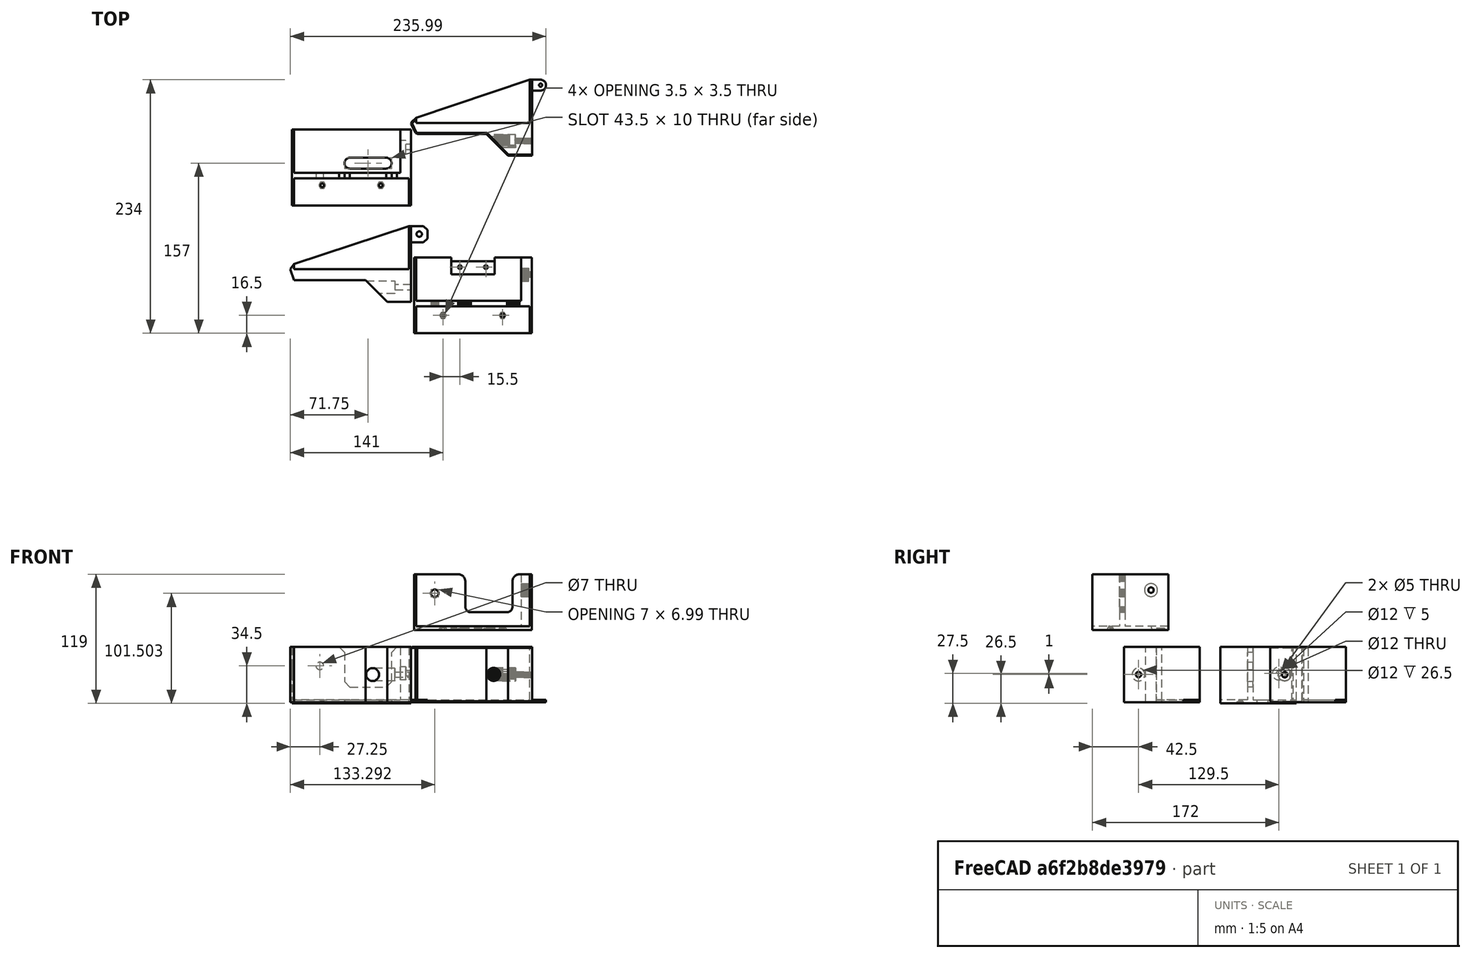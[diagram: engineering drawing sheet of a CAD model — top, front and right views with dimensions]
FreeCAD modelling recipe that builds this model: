
FCSTD DOCUMENT  (FreeCAD 0.19R24291 (Git))
Label: PRUSA-Black-PSU
License: All rights reserved
LicenseURL: http://en.wikipedia.org/wiki/All_rights_reserved
objects: Sketcher::SketchObject×19, PartDesign::Pocket×13, PartDesign::Pad×6, Part::Feature×4, Mesh::Feature×2, Part::Refine×2, PartDesign::Body×2, PartDesign::Chamfer×1
note: 67 computed .brp shape members not serialized (recipe doc carries the construction recipe); baked Part::Feature solids carry a one-line shape summary decoded from their .brp

FEATURE [Mesh::Feature] Top_Bracket_v5
FEATURE [Sketcher::SketchObject] Sketch
  FullyConstrained = true
  MapMode = 5
  Placement = pos=(0,0,0) rot=(1,0,0;1.5708rad)
  Support = -> [XZ_Plane]
  sketch-geometry (4):
    g0: LineSegment StartX=-55 StartY=35 StartZ=0 EndX=55 EndY=35 EndZ=0
    g1: LineSegment StartX=55 StartY=35 StartZ=0 EndX=55 EndY=-35 EndZ=0
    g2: LineSegment StartX=55 StartY=-35 StartZ=0 EndX=-55 EndY=-35 EndZ=0
    g3: LineSegment StartX=-55 StartY=-35 StartZ=0 EndX=-55 EndY=35 EndZ=0
  constraints (10):
    c: Coincident(g0,g1)
    c: Coincident(g1,g2)
    c: Coincident(g2,g3)
    c: Coincident(g3,g0)
    c: Horizontal(g2)
    c: Vertical(g3)
    c: Symmetric(g0,g0,g-2)
    c: Symmetric(g0,g1,g-1)
    c: DistanceX(g2,g2) = 110
    c: DistanceY(g3,g3) = 70
FEATURE [Part::Feature] Top_Bracket_v5001
  shape: bbox 108.5 x 51.5 x 70 mm, 1624 faces, 0 solids (baked)
FEATURE [Part::Refine] Top_Bracket_v5001001
  Source = -> Top_Bracket_v5001
FEATURE [Part::Feature] Top_Bracket_v5001001_solid  label="Top_Bracket_v5001001 (Solid)"
  Placement = pos=(0,0,0) rot=(0,0.707107,0.707107;3.14159rad)
  shape: bbox 108.5 x 70 x 51.5 mm, 406 faces (baked)
FEATURE [Sketcher::SketchObject] Sketch001
  FullyConstrained = true
  MapMode = 5
  Support = -> [XY_Plane]
  sketch-geometry (8):
    g0: LineSegment StartX=53 StartY=-52 StartZ=0 EndX=55 EndY=-52 EndZ=0
    g1: LineSegment StartX=55 StartY=-52 StartZ=0 EndX=55 EndY=1.819e-12 EndZ=0
    g2: LineSegment StartX=55 StartY=1.819e-12 StartZ=0 EndX=53 EndY=1.819e-12 EndZ=0
    g3: LineSegment StartX=53 StartY=1.819e-12 StartZ=0 EndX=53 EndY=-52 EndZ=0
    g4: LineSegment StartX=-53 StartY=-52 StartZ=0 EndX=-55 EndY=-52 EndZ=0
    g5: LineSegment StartX=-55 StartY=-52 StartZ=0 EndX=-55 EndY=0 EndZ=0
    g6: LineSegment StartX=-55 StartY=0 StartZ=0 EndX=-53 EndY=0 EndZ=0
    g7: LineSegment StartX=-53 StartY=0 StartZ=0 EndX=-53 EndY=-52 EndZ=0
  constraints (23):
    c: Coincident(g0,g1)
    c: Coincident(g1,g2)
    c: Coincident(g2,g3)
    c: Coincident(g3,g0)
    c: Horizontal(g0)
    c: Horizontal(g2)
    c: Vertical(g1)
    c: Vertical(g3)
    c: DistanceX(g2,g2) = 2
    c: Coincident(g4,g5)
    c: Coincident(g5,g6)
    c: Coincident(g6,g7)
    c: Coincident(g7,g4)
    c: Horizontal(g4)
    c: Horizontal(g6)
    c: Vertical(g5)
    c: Vertical(g7)
    c: Equal(g6,g2)
    c: DistanceY(g7,g7) = 52
    c: Equal(g3,g7)
    c: PointOnObject(g5,g-1)
    c: Symmetric(g4,g0,g-2)
    c: DistanceX(g6,g2) = 106
FEATURE [Sketcher::SketchObject] Sketch002
  FullyConstrained = true
  MapMode = 5
  Placement = pos=(0,0,0) rot=(1,0,0;1.5708rad)
  Support = -> [XZ_Plane]
  sketch-geometry (4):
    g0: LineSegment StartX=45 StartY=35 StartZ=0 EndX=55 EndY=35 EndZ=0
    g1: LineSegment StartX=55 StartY=35 StartZ=0 EndX=55 EndY=-10 EndZ=0
    g2: LineSegment StartX=55 StartY=-10 StartZ=0 EndX=45 EndY=-10 EndZ=0
    g3: LineSegment StartX=45 StartY=-10 StartZ=0 EndX=45 EndY=35 EndZ=0
  constraints (12):
    c: Coincident(g0,g1)
    c: Coincident(g1,g2)
    c: Coincident(g2,g3)
    c: Coincident(g3,g0)
    c: Horizontal(g0)
    c: Horizontal(g2)
    c: Vertical(g1)
    c: Vertical(g3)
    c: DistanceX(g0,g0) = 10
    c: DistanceY(g3,g3) = 45
    c: DistanceY(g-1,g0) = 35
    c: DistanceX(g-1,g0) = 55
FEATURE [Sketcher::SketchObject] Sketch003
  FullyConstrained = true
  MapMode = 5
  Placement = pos=(0,0,0) rot=(1,0,0;1.5708rad)
  Support = -> [XZ_Plane]
  sketch-geometry (4):
    g0: LineSegment StartX=-55 StartY=-5 StartZ=0 EndX=55 EndY=-5 EndZ=0
    g1: LineSegment StartX=55 StartY=-5 StartZ=0 EndX=55 EndY=-10 EndZ=0
    g2: LineSegment StartX=55 StartY=-10 StartZ=0 EndX=-55 EndY=-10 EndZ=0
    g3: LineSegment StartX=-55 StartY=-10 StartZ=0 EndX=-55 EndY=-5 EndZ=0
  constraints (11):
    c: Coincident(g0,g1)
    c: Coincident(g1,g2)
    c: Coincident(g2,g3)
    c: Coincident(g3,g0)
    c: Horizontal(g0)
    c: Vertical(g1)
    c: Vertical(g3)
    c: DistanceY(g1,g1) = 5
    c: Symmetric(g1,g2,g-2)
    c: DistanceX(g0,g0) = 110
    c: DistanceY(g1,g-1) = 10
FEATURE [Mesh::Feature] PSU_Bottom_Bracket
FEATURE [Part::Feature] PSU_Bottom_Bracket001
  shape: bbox 124.5 x 70 x 51 mm, 1006 faces, 0 solids (baked)
FEATURE [Part::Refine] PSU_Bottom_Bracket001001
  Source = -> PSU_Bottom_Bracket001
FEATURE [Part::Feature] PSU_Bottom_Bracket001001_solid  label="PSU_Bottom_Bracket001001 (Solid)"
  Placement = pos=(-12.5,149,-66.5) rot=(0,0,1;0rad)
  shape: bbox 124.5 x 70 x 51 mm, 605 faces (baked)
FEATURE [PartDesign::Pad] Pad
  Direction = (1,1,1)
  Length = 3
  Length2 = 100
  Placement = pos=(0,0,0) rot=(1,0,0;1.5708rad)
  Profile = -> Sketch
  Type = 0
FEATURE [PartDesign::Pad] Pad001
  BaseFeature = -> Pad
  Direction = (1,1,1)
  Length = 70
  Length2 = 100
  Midplane = true
  Placement = pos=(0,0,0) rot=(1,0,0;1.5708rad)
  Profile = -> Sketch001
  Type = 0
FEATURE [PartDesign::Pad] Pad002
  BaseFeature = -> Pad001
  Direction = (1,1,1)
  Length = 52
  Length2 = 100
  Placement = pos=(0,0,0) rot=(1,0,0;1.5708rad)
  Profile = -> Sketch002
  Type = 0
FEATURE [PartDesign::Pad] Pad003
  BaseFeature = -> Pad002
  Direction = (1,1,1)
  Length = 52
  Length2 = 100
  Placement = pos=(0,0,0) rot=(1,0,0;1.5708rad)
  Profile = -> Sketch003
  Type = 0
FEATURE [Sketcher::SketchObject] Sketch004
  ExternalGeometry = -> [Pad003]
  FullyConstrained = true
  MapMode = 5
  Placement = pos=(0,0,-5) rot=(0,0,1;3.14159rad)
  Support = -> [Pad003]
  sketch-geometry (7):
    g0: LineSegment StartX=-37 StartY=52 StartZ=0 EndX=6.5 EndY=52 EndZ=0
    g1: LineSegment StartX=6.5 StartY=52 StartZ=0 EndX=6.5 EndY=15 EndZ=0
    g2: LineSegment StartX=6.5 StartY=15 StartZ=0 EndX=-37 EndY=15 EndZ=0
    g3: LineSegment StartX=-37 StartY=15 StartZ=0 EndX=-37 EndY=52 EndZ=0
    g4: Circle CenterX=29.25 CenterY=34.5 CenterZ=0 NormalX=0 NormalY=0 NormalZ=1 AngleXU=0 Radius=3.5
    g5: LineSegment StartX=29.25 StartY=34.5 StartZ=0 EndX=29.25 EndY=52 EndZ=0
    g6: LineSegment StartX=29.25 StartY=34.5 StartZ=0 EndX=53 EndY=34.5 EndZ=0
  constraints (22):
    c: Coincident(g0,g1)
    c: Coincident(g1,g2)
    c: Coincident(g2,g3)
    c: Coincident(g3,g0)
    c: Horizontal(g0)
    c: Horizontal(g2)
    c: Vertical(g1)
    c: Vertical(g3)
    c: DistanceX(g0,g0) = 43.5
    c: DistanceY(g3,g3) = 37
    c: Radius(g4) = 3.5
    c: Coincident(g5,g4)
    c: Vertical(g5)
    c: Coincident(g6,g4)
    c: Horizontal(g6)
    c: DistanceX(g6,g6) = 23.75
    c: Horizontal(g0,g-3)
    c: DistanceX(g-3,g0) = 8
    c: Horizontal(g5,g-4)
    c: PointOnObject(g6,g-4)
    c: DistanceY(g5,g5) = 17.5
    c: DistanceX(g-1,g0) = 6.5
FEATURE [PartDesign::Pocket] Pocket
  BaseFeature = -> Pad003
  Length = 5
  Length2 = 100
  Placement = pos=(0,0,0) rot=(1,0,0;1.5708rad)
  Profile = -> Sketch004
  Type = 0
FEATURE [Sketcher::SketchObject] Sketch005
  ExternalGeometry = -> [Pocket]
  FullyConstrained = true
  MapMode = 5
  Placement = pos=(45,0,0) rot=(0.707107,0,-0.707107;3.14159rad)
  Support = -> [Pocket]
  sketch-geometry (4):
    g0: Circle CenterX=-19 CenterY=27.5 CenterZ=0 NormalX=0 NormalY=0 NormalZ=1 AngleXU=0 Radius=2.5
    g1: LineSegment StartX=-19 StartY=27.5 StartZ=0 EndX=-35 EndY=27.5 EndZ=0
    g2: LineSegment StartX=-19 StartY=27.5 StartZ=0 EndX=-19 EndY=3 EndZ=0
    g3: LineSegment StartX=-19 StartY=27.5 StartZ=0 EndX=-19 EndY=52 EndZ=0
  constraints (12):
    c: Radius(g0) = 2.5
    c: Coincident(g1,g0)
    c: Horizontal(g1)
    c: Coincident(g2,g0)
    c: Vertical(g2)
    c: DistanceX(g1,g1) = 16
    c: Coincident(g3,g0)
    c: Vertical(g3)
    c: Equal(g3,g2)
    c: Horizontal(g3,g-3)
    c: Horizontal(g2,g-3)
    c: PointOnObject(g1,g-3)
FEATURE [PartDesign::Pocket] Pocket001
  BaseFeature = -> Pocket
  Length = 10
  Length2 = 100
  Placement = pos=(0,0,0) rot=(1,0,0;1.5708rad)
  Profile = -> Sketch005
  Type = 0
FEATURE [Sketcher::SketchObject] Sketch006
  ExternalGeometry = -> [Pocket001]
  FullyConstrained = true
  MapMode = 5
  Placement = pos=(45,0,0) rot=(0.707107,0,-0.707107;3.14159rad)
  Support = -> [Pocket001]
  sketch-geometry (1):
    g0: Circle CenterX=-19 CenterY=27.5 CenterZ=0 NormalX=0 NormalY=0 NormalZ=1 AngleXU=0 Radius=6
  constraints (2):
    c: Radius(g0) = 6
    c: Coincident(g0,g-4)
FEATURE [PartDesign::Pocket] Pocket002
  BaseFeature = -> Pocket001
  Length = 5
  Length2 = 100
  Placement = pos=(0,0,0) rot=(1,0,0;1.5708rad)
  Profile = -> Sketch006
  Type = 0
FEATURE [Sketcher::SketchObject] Sketch011
  ExternalGeometry = -> [Pocket002]
  FullyConstrained = true
  MapMode = 5
  Placement = pos=(45,0,0) rot=(0.707107,0,-0.707107;3.14159rad)
  Support = -> [Pocket002]
  sketch-geometry (1):
    g0: Circle CenterX=-19 CenterY=27.5 CenterZ=0 NormalX=0 NormalY=0 NormalZ=1 AngleXU=0 Radius=6
  constraints (2):
    c: Coincident(g0,g-4)
    c: Equal(g0,g-4)
FEATURE [PartDesign::Pocket] Pocket003
  BaseFeature = -> Pocket002
  Length = 150
  Length2 = 100
  Placement = pos=(0,0,0) rot=(1,0,0;1.5708rad)
  Profile = -> Sketch011
  Reversed = true
  Type = 0
FEATURE [Sketcher::SketchObject] Sketch007
  ExternalGeometry = -> [Pocket003]
  FullyConstrained = true
  MapMode = 5
  Placement = pos=(0,0,0) rot=(1,0,0;1.5708rad)
  Support = -> [XZ_Plane]
  sketch-geometry (4):
    g0: Circle CenterX=-27 CenterY=-16.5 CenterZ=0 NormalX=0 NormalY=0 NormalZ=1 AngleXU=0 Radius=1.65
    g1: LineSegment StartX=-27 StartY=-16.5 StartZ=0 EndX=-55 EndY=-16.5 EndZ=0
    g2: LineSegment StartX=-27 StartY=-16.5 StartZ=0 EndX=-27 EndY=-35 EndZ=0
    g3: Circle CenterX=27 CenterY=-16.5 CenterZ=0 NormalX=0 NormalY=0 NormalZ=1 AngleXU=0 Radius=1.65
  constraints (11):
    c: Radius(g0) = 1.65
    c: Coincident(g1,g0)
    c: Horizontal(g1)
    c: Coincident(g2,g0)
    c: Vertical(g2)
    c: DistanceY(g2,g2) = 18.5
    c: DistanceX(g1,g1) = 28
    c: Equal(g3,g0)
    c: Symmetric(g3,g0,g-2)
    c: Horizontal(g-3,g2)
    c: PointOnObject(g1,g-3)
FEATURE [Sketcher::SketchObject] Sketch008
  ExternalGeometry = -> [Sketch007]
  FullyConstrained = true
  MapMode = 5
  Placement = pos=(0,0,0) rot=(1,0,0;1.5708rad)
  Support = -> [XZ_Plane]
  sketch-geometry (14):
    g0: LineSegment StartX=-25.35 StartY=-13.6421 StartZ=0 EndX=-28.65 EndY=-13.6421 EndZ=0
    g1: LineSegment StartX=-28.65 StartY=-13.6421 StartZ=0 EndX=-30.3 EndY=-16.5 EndZ=0
    g2: LineSegment StartX=-30.3 StartY=-16.5 StartZ=0 EndX=-28.65 EndY=-19.3579 EndZ=0
    g3: LineSegment StartX=-28.65 StartY=-19.3579 StartZ=0 EndX=-25.35 EndY=-19.3579 EndZ=0
    g4: LineSegment StartX=-25.35 StartY=-19.3579 StartZ=0 EndX=-23.7 EndY=-16.5 EndZ=0
    g5: LineSegment StartX=-23.7 StartY=-16.5 StartZ=0 EndX=-25.35 EndY=-13.6421 EndZ=0
    g6: Circle CenterX=-27 CenterY=-16.5 CenterZ=0 NormalX=0 NormalY=0 NormalZ=1 AngleXU=0 Radius=3.3
    g7: LineSegment StartX=30.3 StartY=-16.5 StartZ=0 EndX=28.65 EndY=-13.6421 EndZ=0
    g8: LineSegment StartX=28.65 StartY=-13.6421 StartZ=0 EndX=25.35 EndY=-13.6421 EndZ=0
    g9: LineSegment StartX=25.35 StartY=-13.6421 StartZ=0 EndX=23.7 EndY=-16.5 EndZ=0
    g10: LineSegment StartX=23.7 StartY=-16.5 StartZ=0 EndX=25.35 EndY=-19.3579 EndZ=0
    g11: LineSegment StartX=25.35 StartY=-19.3579 StartZ=0 EndX=28.65 EndY=-19.3579 EndZ=0
    g12: LineSegment StartX=28.65 StartY=-19.3579 StartZ=0 EndX=30.3 EndY=-16.5 EndZ=0
    g13: Circle CenterX=27 CenterY=-16.5 CenterZ=0 NormalX=0 NormalY=0 NormalZ=1 AngleXU=0 Radius=3.3
  constraints (34):
    c: Coincident(g0,g1)
    c: Coincident(g1,g2)
    c: Coincident(g2,g3)
    c: Coincident(g3,g4)
    c: Coincident(g4,g5)
    c: Coincident(g5,g0)
    c: Equal(g0, g1-g5) x5
    c: PointOnObject(g0,g6)
    c: PointOnObject(g1,g6)
    c: PointOnObject(g2,g6)
    c: PointOnObject(g3,g6)
    c: PointOnObject(g4,g6)
    c: PointOnObject(g5,g6)
    c: Horizontal(g0)
    c: DistanceX(g1,g4) = 6.6
    c: Coincident(g6,g-3)
    c: Coincident(g7,g8)
    c: Coincident(g8,g9)
    c: Coincident(g9,g10)
    c: Coincident(g10,g11)
    c: Coincident(g11,g12)
    c: Coincident(g12,g7)
    c: Equal(g7, g8-g12) x5
    c: PointOnObject(g7,g13)
    c: PointOnObject(g8,g13)
    c: PointOnObject(g9,g13)
    c: PointOnObject(g10,g13)
    c: PointOnObject(g11,g13)
    c: PointOnObject(g12,g13)
    c: Horizontal(g8)
    c: Equal(g8,g3)
    c: Symmetric(g13,g6,g-2)
    c: Distance(g2,g4) = 5.71577
    c: DistanceX(g3,g3) = 3.3
FEATURE [PartDesign::Pocket] Pocket004
  BaseFeature = -> Pocket003
  Length = 5
  Length2 = 100
  Placement = pos=(0,0,0) rot=(1,0,0;1.5708rad)
  Profile = -> Sketch007
  Reversed = true
  Type = 0
FEATURE [PartDesign::Pocket] Pocket005
  BaseFeature = -> Pocket004
  Length = 1.4
  Length2 = 100
  Placement = pos=(0,0,0) rot=(1,0,0;1.5708rad)
  Profile = -> Sketch008
  Reversed = true
  Type = 0
FEATURE [Sketcher::SketchObject] Sketch009
  ExternalGeometry = -> [Pocket005]
  FullyConstrained = true
  MapMode = 5
  Placement = pos=(0,-1.4,-3e-16) rot=(-1,0,0;1.5708rad)
  Support = -> [Pocket005]
  sketch-geometry (8):
    g0: LineSegment StartX=-28.65 StartY=19.3579 StartZ=0 EndX=-28.65 EndY=13.6421 EndZ=0
    g1: LineSegment StartX=-25.35 StartY=19.3579 StartZ=0 EndX=-25.35 EndY=13.6421 EndZ=0
    g2: LineSegment StartX=-25.35 StartY=19.3579 StartZ=0 EndX=-28.65 EndY=19.3579 EndZ=0
    g3: LineSegment StartX=-28.65 StartY=13.6421 StartZ=0 EndX=-25.35 EndY=13.6421 EndZ=0
    g4: LineSegment StartX=25.35 StartY=19.3579 StartZ=0 EndX=28.65 EndY=19.3579 EndZ=0
    g5: LineSegment StartX=28.65 StartY=19.3579 StartZ=0 EndX=28.65 EndY=13.6421 EndZ=0
    g6: LineSegment StartX=28.65 StartY=13.6421 StartZ=0 EndX=25.35 EndY=13.6421 EndZ=0
    g7: LineSegment StartX=25.35 StartY=13.6421 StartZ=0 EndX=25.35 EndY=19.3579 EndZ=0
  constraints (20):
    c: Coincident(g2,g1)
    c: Coincident(g2,g0)
    c: Coincident(g3,g0)
    c: Coincident(g3,g1)
    c: Coincident(g4,g5)
    c: Coincident(g5,g6)
    c: Coincident(g6,g7)
    c: Coincident(g7,g4)
    c: Horizontal(g4)
    c: Horizontal(g6)
    c: Vertical(g5)
    c: Vertical(g7)
    c: Vertical(g0)
    c: Vertical(g1)
    c: Horizontal(g3)
    c: Horizontal(g2)
    c: Coincident(g-5,g4)
    c: Coincident(g5,g-6)
    c: Coincident(g0,g-3)
    c: Coincident(g1,g-4)
FEATURE [PartDesign::Pocket] Pocket006
  BaseFeature = -> Pocket005
  Length = 0.2
  Length2 = 100
  Placement = pos=(0,0,0) rot=(1,0,0;1.5708rad)
  Profile = -> Sketch009
  Type = 0
FEATURE [Sketcher::SketchObject] Sketch010
  ExternalGeometry = -> [Pocket006]
  FullyConstrained = true
  MapMode = 5
  Placement = pos=(0,-1.6,-3e-16) rot=(-1,0,0;1.5708rad)
  Support = -> [Pocket006]
  sketch-geometry (8):
    g0: LineSegment StartX=25.35 StartY=18.15 StartZ=0 EndX=28.65 EndY=18.15 EndZ=0
    g1: LineSegment StartX=28.65 StartY=18.15 StartZ=0 EndX=28.65 EndY=14.85 EndZ=0
    g2: LineSegment StartX=28.65 StartY=14.85 StartZ=0 EndX=25.35 EndY=14.85 EndZ=0
    g3: LineSegment StartX=25.35 StartY=14.85 StartZ=0 EndX=25.35 EndY=18.15 EndZ=0
    g4: LineSegment StartX=-28.65 StartY=18.15 StartZ=0 EndX=-25.35 EndY=18.15 EndZ=0
    g5: LineSegment StartX=-25.35 StartY=18.15 StartZ=0 EndX=-25.35 EndY=14.85 EndZ=0
    g6: LineSegment StartX=-25.35 StartY=14.85 StartZ=0 EndX=-28.65 EndY=14.85 EndZ=0
    g7: LineSegment StartX=-28.65 StartY=14.85 StartZ=0 EndX=-28.65 EndY=18.15 EndZ=0
  constraints (24):
    c: Coincident(g0,g1)
    c: Coincident(g1,g2)
    c: Coincident(g2,g3)
    c: Coincident(g3,g0)
    c: Horizontal(g0)
    c: Horizontal(g2)
    c: Vertical(g1)
    c: Vertical(g3)
    c: Equal(g3,g0)
    c: Coincident(g4,g5)
    c: Coincident(g5,g6)
    c: Coincident(g6,g7)
    c: Coincident(g7,g4)
    c: Horizontal(g4)
    c: Horizontal(g6)
    c: Vertical(g5)
    c: Vertical(g7)
    c: Equal(g4,g7)
    c: PointOnObject(g-3,g5)
    c: PointOnObject(g-3,g7)
    c: Tangent(g-3,g4)
    c: PointOnObject(g-4,g3)
    c: PointOnObject(g-4,g1)
    c: Tangent(g0,g-4)
FEATURE [PartDesign::Pocket] Pocket007
  BaseFeature = -> Pocket006
  Length = 0.2
  Length2 = 100
  Placement = pos=(0,0,0) rot=(1,0,0;1.5708rad)
  Profile = -> Sketch010
  Type = 0
FEATURE [Sketcher::SketchObject] Sketch012
  FullyConstrained = true
  MapMode = 5
  Support = -> [XY_Plane001]
  sketch-geometry (8):
    g0: LineSegment StartX=40 StartY=50 StartZ=0 EndX=-66 EndY=15 EndZ=0
    g1: LineSegment StartX=-69.5 StartY=10 StartZ=0 EndX=-66 EndY=0 EndZ=0
    g2: LineSegment StartX=-66 StartY=0 StartZ=0 EndX=0 EndY=0 EndZ=0
    g3: LineSegment StartX=0 StartY=0 StartZ=0 EndX=20 EndY=-20 EndZ=0
    g4: LineSegment StartX=20 StartY=-20 StartZ=0 EndX=42 EndY=-20 EndZ=0
    g5: LineSegment StartX=42 StartY=-20 StartZ=0 EndX=42 EndY=50 EndZ=0
    g6: LineSegment StartX=42 StartY=50 StartZ=0 EndX=40 EndY=50 EndZ=0
    g7: LineSegment StartX=-66 StartY=15 StartZ=0 EndX=-69.5 EndY=10 EndZ=0
  constraints (23):
    c: Coincident(g1,g2)
    c: Horizontal(g2)
    c: Coincident(g2,g3)
    c: Coincident(g3,g4)
    c: Horizontal(g4)
    c: Coincident(g4,g5)
    c: Vertical(g5)
    c: Coincident(g6,g5)
    c: Coincident(g6,g0)
    c: Horizontal(g6)
    c: DistanceX(g6,g6) = 2
    c: DistanceY(g5,g5) = 70
    c: DistanceX(g4,g4) = 22
    c: Coincident(g7,g0)
    c: Coincident(g7,g1)
    c: DistanceX(g0,g0) = 106
    c: DistanceY(g0,g0) = 35
    c: DistanceX(g2,g3) = 20
    c: DistanceY(g3,g2) = 20
    c: DistanceX(g1,g1) = 3.5
    c: DistanceY(g1,g1) = 10
    c: Coincident(g2,g-1)
    c: Vertical(g0,g1)
FEATURE [PartDesign::Pad] Pad004
  Direction = (1,1,1)
  Length = 51
  Length2 = 100
  Profile = -> Sketch012
  Type = 0
FEATURE [Sketcher::SketchObject] Sketch013
  ExternalGeometry = -> [Pad004]
  FullyConstrained = true
  MapMode = 5
  Placement = pos=(0,0,51) rot=(0,0,1;0rad)
  Support = -> [Pad004]
  sketch-geometry (4):
    g0: LineSegment StartX=40 StartY=50 StartZ=0 EndX=-66 EndY=15 EndZ=0
    g1: LineSegment StartX=-66 StartY=15 StartZ=0 EndX=-66 EndY=10 EndZ=0
    g2: LineSegment StartX=-66 StartY=10 StartZ=0 EndX=40 EndY=10 EndZ=0
    g3: LineSegment StartX=40 StartY=10 StartZ=0 EndX=40 EndY=50 EndZ=0
  constraints (12):
    c: Coincident(g0,g1)
    c: Coincident(g1,g2)
    c: Horizontal(g2)
    c: Coincident(g2,g3)
    c: Vertical(g3)
    c: DistanceX(g2,g-3) = 2
    c: Horizontal(g3,g-3)
    c: Coincident(g0,g3)
    c: DistanceX(g2,g2) = 106
    c: Vertical(g1)
    c: DistanceY(g1,g1) = 5
    c: DistanceY(g3,g3) = 40
FEATURE [PartDesign::Pocket] Pocket008
  BaseFeature = -> Pad004
  Length = 49
  Length2 = 100
  Profile = -> Sketch013
  Type = 0
FEATURE [Sketcher::SketchObject] Sketch014
  ExternalGeometry = -> [Pocket008]
  FullyConstrained = true
  MapMode = 5
  Placement = pos=(42,0,0) rot=(0.57735,0.57735,0.57735;2.0944rad)
  Support = -> [Pocket008]
  sketch-geometry (2):
    g0: Circle CenterX=-6.5 CenterY=25.5 CenterZ=0 NormalX=0 NormalY=0 NormalZ=1 AngleXU=0 Radius=2.5
    g1: LineSegment StartX=-20 StartY=25.5 StartZ=0 EndX=-6.5 EndY=25.5 EndZ=0
  constraints (5):
    c: Radius(g0) = 2.5
    c: Coincident(g1,g0)
    c: Horizontal(g1)
    c: Symmetric(g-3,g-3,g1)
    c: DistanceX(g1,g1) = 13.5
FEATURE [PartDesign::Pocket] Pocket009
  BaseFeature = -> Pocket008
  Length = 5
  Length2 = 100
  Profile = -> Sketch014
  Type = 1
FEATURE [Sketcher::SketchObject] Sketch015
  ExternalGeometry = -> [Pocket009]
  FullyConstrained = true
  MapMode = 5
  Placement = pos=(0,0,0) rot=(0.57735,0.57735,0.57735;2.0944rad)
  Support = -> [YZ_Plane001]
  sketch-geometry (1):
    g0: Circle CenterX=-6.5 CenterY=25.5 CenterZ=0 NormalX=0 NormalY=0 NormalZ=1 AngleXU=0 Radius=6
  constraints (2):
    c: Coincident(g0,g-3)
    c: Radius(g0) = 6
FEATURE [PartDesign::Pocket] Pocket010
  BaseFeature = -> Pocket009
  Length = 27
  Length2 = 100
  Profile = -> Sketch015
  Reversed = true
  Type = 0
FEATURE [Sketcher::SketchObject] Sketch016
  ExternalGeometry = -> [Pocket010]
  FullyConstrained = true
  MapMode = 5
  Support = -> [XY_Plane001]
  sketch-geometry (6):
    g0: LineSegment StartX=53.4645 StartY=50 StartZ=0 EndX=42 EndY=50 EndZ=0
    g1: LineSegment StartX=42 StartY=50 StartZ=0 EndX=42 EndY=35 EndZ=0
    g2: LineSegment StartX=42 StartY=35 StartZ=0 EndX=53.4645 EndY=35 EndZ=0
    g3: LineSegment StartX=57 StartY=38.5355 StartZ=0 EndX=57 EndY=46.4645 EndZ=0
    g4: LineSegment StartX=53.4645 StartY=50 StartZ=0 EndX=57 EndY=46.4645 EndZ=0
    g5: LineSegment StartX=57 StartY=38.5355 StartZ=0 EndX=53.4645 EndY=35 EndZ=0
  constraints (17):
    c: Coincident(g0,g1)
    c: Coincident(g1,g2)
    c: Horizontal(g0)
    c: Horizontal(g2)
    c: Vertical(g1)
    c: Vertical(g3)
    c: Coincident(g0,g-3)
    c: Equal(g4,g5)
    c: Angle(g5,g2) = 2.35619
    c: Distance(g5) = 5
    c: Vertical(g4,g5)
    c: Coincident(g3,g4)
    c: Coincident(g0,g4)
    c: Coincident(g3,g5)
    c: Coincident(g2,g5)
    c: DistanceY(g2,g0) = 15
    c: DistanceX(g1,g3) = 15
FEATURE [PartDesign::Pad] Pad005
  BaseFeature = -> Pocket010
  Direction = (1,1,1)
  Length = 2
  Length2 = 100
  Profile = -> Sketch016
  Type = 0
FEATURE [Sketcher::SketchObject] Sketch017
  ExternalGeometry = -> [Pad005]
  FullyConstrained = true
  MapMode = 5
  Placement = pos=(0,0,2) rot=(0,0,1;0rad)
  Support = -> [Pad005]
  sketch-geometry (3):
    g0: Circle CenterX=49.5 CenterY=42.5 CenterZ=0 NormalX=0 NormalY=0 NormalZ=1 AngleXU=0 Radius=2.5
    g1: LineSegment StartX=49.5 StartY=42.5 StartZ=0 EndX=42 EndY=42.5 EndZ=0
    g2: LineSegment StartX=49.5 StartY=42.5 StartZ=0 EndX=57 EndY=42.5 EndZ=0
  constraints (8):
    c: Radius(g0) = 2.5
    c: Coincident(g1,g0)
    c: Horizontal(g1)
    c: Symmetric(g-3,g-5,g1)
    c: Coincident(g2,g0)
    c: PointOnObject(g2,g-6)
    c: Horizontal(g2)
    c: Equal(g2,g1)
FEATURE [PartDesign::Pocket] Pocket011
  BaseFeature = -> Pad005
  Length = 5
  Length2 = 100
  Profile = -> Sketch017
  Type = 0
FEATURE [PartDesign::Body] Body001  label="Bottom_Bracket"
  Group = -> [Sketch012,Pad004,Sketch013,Pocket008,Sketch014,Pocket009,Sketch015,Pocket010,Sketch016,Pad005,Sketch017,Pocket011]
  Origin = -> Origin001
  Placement = pos=(-99,14,-66.5) rot=(0,0,1;0rad)
  Tip = -> Pocket011
FEATURE [PartDesign::Chamfer] Chamfer
  Angle = 45
  Base = -> Pocket007 [Edge98,Edge93,Edge96,Edge94]
  BaseFeature = -> Pocket007
  ChamferType = 0
  FlipDirection = false
  Placement = pos=(0,0,0) rot=(1,0,0;1.5708rad)
  Size = 5
  Size2 = 1
  SupportTransform = false
FEATURE [Sketcher::SketchObject] Sketch018
  FullyConstrained = true
  MapMode = 5
  Placement = pos=(0,0,0) rot=(1,0,0;1.5708rad)
  Support = -> [XZ_Plane]
  sketch-geometry (5):
    g0: ArcOfCircle CenterX=-1.5 CenterY=4 CenterZ=0 NormalX=0 NormalY=0 NormalZ=1 AngleXU=0 Radius=5 StartAngle=1.5708 EndAngle=4.71239
    g1: ArcOfCircle CenterX=32 CenterY=4 CenterZ=0 NormalX=0 NormalY=0 NormalZ=1 AngleXU=0 Radius=5 StartAngle=4.71239 EndAngle=7.85398
    g2: LineSegment StartX=-1.5 StartY=-1 StartZ=0 EndX=32 EndY=-1 EndZ=0
    g3: LineSegment StartX=-1.5 StartY=9 StartZ=0 EndX=32 EndY=9 EndZ=0
    g4: LineSegment StartX=37 StartY=4 StartZ=0 EndX=-6.5 EndY=4 EndZ=0
  constraints (14):
    c: Tangent(g0,g3) = 1.5708
    c: Tangent(g0,g2) = -1.5708
    c: Tangent(g2,g1) = -1.5708
    c: Tangent(g3,g1) = 1.5708
    c: Horizontal(g2)
    c: Equal(g0,g1)
    c: DistanceY(g0,g0) = 10
    c: DistanceY(g-1,g0) = 4
    c: PointOnObject(g4,g1)
    c: PointOnObject(g4,g0)
    c: Horizontal(g4)
    c: PointOnObject(g1,g4)
    c: DistanceX(g4,g4) = 43.5
    c: DistanceX(g4,g-1) = 6.5
FEATURE [PartDesign::Pocket] Pocket012
  BaseFeature = -> Chamfer
  Length = 5
  Length2 = 100
  Placement = pos=(0,0,0) rot=(1,0,0;1.5708rad)
  Profile = -> Sketch018
  Reversed = true
  Type = 0
FEATURE [PartDesign::Body] Body  label="Top_Bracket"
  Group = -> [Sketch,Sketch001,Sketch002,Sketch003,Sketch004,Sketch005,Sketch006,Sketch007,Sketch008,Sketch009,Sketch010,Pad,Pad001,Pad002,Pad003,Pocket,Pocket001,Pocket002,Sketch011,Pocket003,Pocket004,Pocket005,Pocket006,Pocket007,Chamfer,Sketch018,Pocket012]
  Origin = -> Origin
  Placement = pos=(-112,118,-67.5) rot=(-1,0,0;1.5708rad)
  Tip = -> Pocket012
